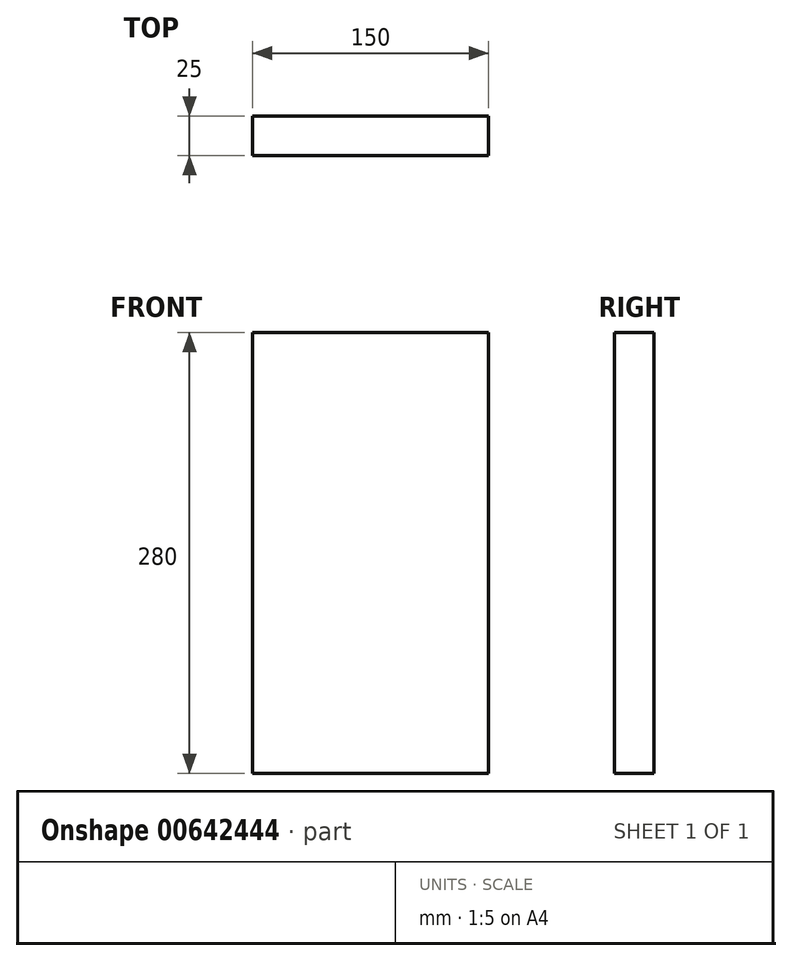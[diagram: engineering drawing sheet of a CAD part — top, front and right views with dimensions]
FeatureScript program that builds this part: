
annotation { "Feature Type Name" : "Feature", "Feature Type Description" : "" }
export const myFeature = defineFeature(function(context is Context, id is Id, definition is map)
    precondition{}
    {
        {
            var Q0;
            Q0=qCreatedBy(makeId("Top.planeOp"),FACE);
            var sketch = newSketch(context, id + "F0", { "sketchPlane" : qUnion([Q0])});
            skLineSegment(sketch, "E0.bottom", {"start": v(-75, 12.5) * mm, "end": v(75, 12.5) * mm});
            skLineSegment(sketch, "E0.top", {"start": v(-75, -12.5) * mm, "end": v(75, -12.5) * mm});
            skLineSegment(sketch, "E0.left", {"start": v(-75, 12.5) * mm, "end": v(-75, -12.5) * mm});
            skLineSegment(sketch, "E0.right", {"start": v(75, 12.5) * mm, "end": v(75, -12.5) * mm});
            skPoint(sketch, "E0.middle", {"position": v(0, 0) * mm});
            skSolve(sketch);
        }
        {
            var Q0;
            Q0=makeQuery(id+"F0.imprint","IMPRINT",FACE,{"disambiguationData":[TD([[makeQuery(id+"F0.imprint","IMPRINT",EDGE,{"derivedFrom":sQuery(id+"F0.wireOp",EDGE,"E0.bottom")}),-1.0]])]});
            extrude(context, id + "F1", {"entities" : qUnion([Q0]), "depth" : 200 * mm, "offsetDistance" : 25 * mm});
        }
        {
            var Q0;
            Q0=makeQuery(id+"F1.opExtrude","CAP_FACE",FACE,{"disambiguationData":[OSD([sQuery(id+"F0.wireOp",EDGE,"E0.bottom"),sQuery(id+"F0.wireOp",EDGE,"E0.top"),sQuery(id+"F0.wireOp",EDGE,"E0.left"),sQuery(id+"F0.wireOp",EDGE,"E0.right")])],"isStart":true});
            extrude(context, id + "F2", {"entities" : qUnion([Q0]), "operationType" : NewBodyOperationType.ADD, "depth" : 80 * mm, "offsetDistance" : 25 * mm});
        }
    });
